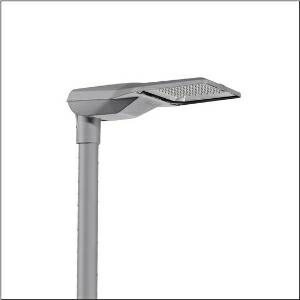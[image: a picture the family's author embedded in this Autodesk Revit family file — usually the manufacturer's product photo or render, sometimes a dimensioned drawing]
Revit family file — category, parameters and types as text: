
# Revit family: streetlight_sl_21_iq_midi___st0_8a_5xe3c41d08mb_0a8a
name_source: partatom
category: Lighting Fixtures
units: mm (PartAtom-declared; Revit-internal decimal feet)

## family parameters
Cut with Voids When Loaded = No
Host = Face
Light Source = No
Part Type = Normal
Room Calculation Point = No
Round Connector Dimension = Use Diameter
Shared = No

## types (1)
- --- (1 x LED, 20360 lm, 146.7 W, 4000K)
    Apparent Load = 147 VA
    CIE Flux Codes = 38 75 97 100 100
    Color Rendering = 70
    Color Temperature = 4000K
    Default Elevation = 1800 mm
    Description = Streetlight SL 21 iQ midi, mast luminaire, primary light control with lens, of PMMA, primary optical cover: cover, of toughened safety glass, transparent, light distribution: ST0.8a, light emission: direct distribution, primary light characteristic: asymmetric, installation type: post-top, side-entry, LED, High Power LED, rated luminous flux: 20.360lm, luminous efficacy: 139lm/W, light colour: 740, colour temperature: 4000K, control gear: iQ-Comfort, control: Auto-Match, Temp-Guard, Lumen-Switch, Night-Set, Smart-Wire, Light-Fading, Desk-Remote (wireless, voltage-free reading and setting of iQ features in the workshop via application-optimized NFC function/RFID function), optimised constant luminous flux control (CLO 2.0), pre-setting: linear dimming characteristic, mains connection: 230..240V, AC, 50/60Hz, start of lifetime: 147W, end of service life: 161W, reduction: 62W, luminaire housing, of diecast aluminium, powder-coated, SITECO metallic grey (DB 702S), corrosivity category C5 high according to DIN EN ISO 12944, please order mast flange separately, inclination adjustable: 0°, 5°, 10°, 15°, sealing non-destructively replaceable, multi-level sealing system, length: 644mm, width: 335mm, height: 110mm, mast flange for spigot size: 42mm (side-entry): 5XC10008XM4, 60/48mm (side-entry/post-top): 5XC10108XM2, 76/60mm (side-entry/post-top): 5XC10108XM1, mounting height: 4..8m, protection rating (complete): IP66, insulation class (complete): insulation class II (safety insulation), certification: CE, ENEC, ENEC+, VDE, impact resistance: IK10, permissible operating ambient temperature for outdoor applications: -40..+50°C, standard-compliant lighting for roads and squares, packaging unit: 1 piece

Light Distribution: ST0.8a
    Height = 111 mm
    Lamp = 1 x LED
    Lamp Light Flux = 20360 lm
    Lamp Power = 146.7 W
    Lamp count = 1
    Length = 644 mm
    Luminous efficacy = 139 lm/W
    Manufacturer = Siteco
    ModVariant = No
    Model = 5XE3C41D08MB
    Number of Poles = 1
    OnlyDefault = Yes
    Power Factor = 1
    Product Name = Streetlight SL 21 iQ midi | ST0.8a
    Product group = mast luminaire | pylon top
    ProductGroupID = 6100
    Protection Class = Protection class II
    Protection Degree = IP 66
    RLX_Detail_Level = 1
    RLX_Emergency_Light_Flux = 0 lm
    RLX_Emergency_Type = 0
    RLX_Emergency_Type_DB = No
    RlxData = <blob elided: 27025 chars, md5=3194335a>
    Socket = socket
    Standby Power = 0 W
    System Light Flux = 20360 lm
    System Power = 147 W
    Type Comments = factory setting: luminous flux: 100 % | dim-lin: 254 | 753 mA
    Type Image = l_1004298.jpg
    URL = http://relux.com
    VarID = @adj_183645
    Voltage = 0 V
    Weight = 0.00 kg
    Width = 336 mm

## geometry (parser evidence)
native form markers: Blend x4, Sweep x11
no freeform markers — native parametric forms only
